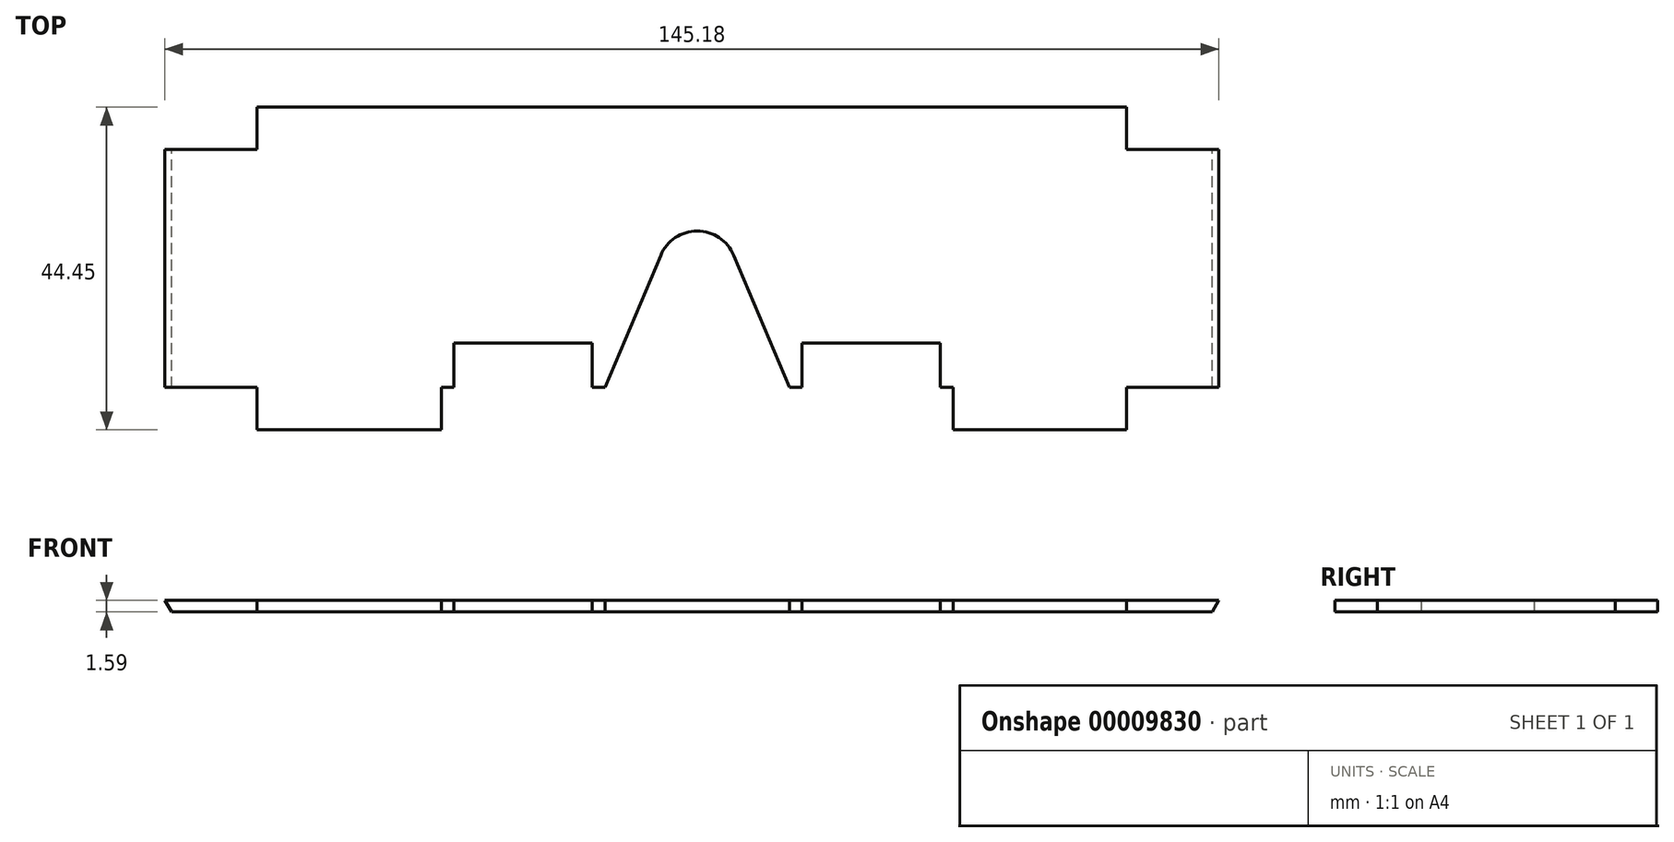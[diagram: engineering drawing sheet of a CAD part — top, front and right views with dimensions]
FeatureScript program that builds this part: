
annotation { "Feature Type Name" : "Feature", "Feature Type Description" : "" }
export const myFeature = defineFeature(function(context is Context, id is Id, definition is map)
    precondition{}
    {
        {
            var Q0;
            Q0=qCreatedBy(makeId("Top.planeOp"),FACE);
            var sketch = newSketch(context, id + "F0", { "sketchPlane" : qUnion([Q0])});
            skLineSegment(sketch, "E0.bottom", {"start": v(-125.55, -13.09) * mm, "end": v(19.63, -13.09) * mm});
            skLineSegment(sketch, "E0.top", {"start": v(-125.55, -57.54) * mm, "end": v(19.63, -57.54) * mm});
            skLineSegment(sketch, "E0.left", {"start": v(-125.55, -13.09) * mm, "end": v(-125.55, -57.54) * mm});
            skLineSegment(sketch, "E0.right", {"start": v(19.63, -13.09) * mm, "end": v(19.63, -57.54) * mm});
            skSolve(sketch);
        }
        {
            var Q0;
            Q0=qSketchRegion(id+"F0",true);
            extrude(context, id + "F1", {"entities" : qUnion([Q0]), "depth" : 1.59 * mm});
        }
        {
            var Q0;
            Q0=makeQuery(id+"F1.opExtrude","CAP_FACE",FACE,{"disambiguationData":[OSD([sQuery(id+"F0.wireOp",EDGE,"E0.bottom"),sQuery(id+"F0.wireOp",EDGE,"E0.top"),sQuery(id+"F0.wireOp",EDGE,"E0.left"),sQuery(id+"F0.wireOp",EDGE,"E0.right")])],"isStart":false});
            var sketch = newSketch(context, id + "F2", { "sketchPlane" : qUnion([Q0])});
            skLineSegment(sketch, "E1.bottom", {"start": v(-112.85, -13.09) * mm, "end": v(-87.45, -13.09) * mm});
            skLineSegment(sketch, "E1.left", {"start": v(-112.85, -13.09) * mm, "end": v(-112.85, -18.93) * mm});
            skLineSegment(sketch, "E2.bottom", {"start": v(-87.45, -13.09) * mm, "end": v(-87.45, -13.09) * mm});
            skLineSegment(sketch, "E3.bottom", {"start": v(-87.45, -13.09) * mm, "end": v(6.93, -13.09) * mm});
            skLineSegment(sketch, "E3.right", {"start": v(6.93, -13.09) * mm, "end": v(6.93, -18.93) * mm});
            skLineSegment(sketch, "E4.bottom", {"start": v(-112.85, -57.54) * mm, "end": v(-87.45, -57.54) * mm});
            skLineSegment(sketch, "E4.left", {"start": v(-112.85, -57.54) * mm, "end": v(-112.85, -51.7) * mm});
            skLineSegment(sketch, "E4.right", {"start": v(-87.45, -57.54) * mm, "end": v(-87.45, -51.7) * mm});
            skLineSegment(sketch, "E5.bottom", {"start": v(-64.92, -57.54) * mm, "end": v(-39.52, -57.54) * mm});
            skLineSegment(sketch, "E5.left", {"start": v(-64.92, -57.54) * mm, "end": v(-64.92, -51.7) * mm});
            skLineSegment(sketch, "E5.right", {"start": v(-39.52, -57.54) * mm, "end": v(-39.52, -51.7) * mm});
            skLineSegment(sketch, "E6.bottom", {"start": v(-17, -57.54) * mm, "end": v(6.93, -57.54) * mm});
            skLineSegment(sketch, "E6.left", {"start": v(-17, -57.54) * mm, "end": v(-17, -51.7) * mm});
            skLineSegment(sketch, "E6.right", {"start": v(6.93, -57.54) * mm, "end": v(6.93, -51.7) * mm});
            skPoint(sketch, "E7", {"position": v(-52.22, -18.93) * mm});
            skPoint(sketch, "E8", {"position": v(-52.22, -51.7) * mm});
            skLineSegment(sketch, "E9", {"start": v(-112.85, -18.93) * mm, "end": v(-125.55, -18.93) * mm});
            skLineSegment(sketch, "E10", {"start": v(-112.85, -51.7) * mm, "end": v(-125.55, -51.7) * mm});
            skLineSegment(sketch, "E11", {"start": v(-125.55, -51.7) * mm, "end": v(-125.55, -18.93) * mm});
            skLineSegment(sketch, "E12", {"start": v(6.93, -18.93) * mm, "end": v(19.63, -18.93) * mm});
            skLineSegment(sketch, "E13", {"start": v(6.93, -51.7) * mm, "end": v(19.63, -51.7) * mm});
            skLineSegment(sketch, "E14", {"start": v(19.63, -51.7) * mm, "end": v(19.63, -18.93) * mm});
            skLineSegment(sketch, "E15", {"start": v(-17, -51.7) * mm, "end": v(-39.52, -51.7) * mm});
            skLineSegment(sketch, "E16", {"start": v(-64.92, -51.7) * mm, "end": v(-87.45, -51.7) * mm});
            skSolve(sketch);
        }
        {
            var Q0;
            {var subQ4=sQuery(id+"F2.wireOp",EDGE,"E1.left");Q0=makeQuery(id+"F2.imprint","IMPRINT",FACE,{"disambiguationData":[TD([[makeQuery(id+"F2.imprint","IMPRINT",EDGE,{"derivedFrom":subQ4}),-1.0]])]});}
            var Q1;
            {var subQ2=sQuery(id+"F2.wireOp",EDGE,"E1.right");Q1=makeQuery(id+"F2.imprint","IMPRINT",FACE,{"disambiguationData":[TD([[makeQuery(id+"F2.imprint","IMPRINT",EDGE,{"derivedFrom":subQ2}),1.0]])]});}
            var Q2;
            {var subQ2=sQuery(id+"F2.wireOp",EDGE,"E2.right");Q2=makeQuery(id+"F2.imprint","IMPRINT",FACE,{"disambiguationData":[TD([[makeQuery(id+"F2.imprint","IMPRINT",EDGE,{"derivedFrom":subQ2}),1.0]])]});}
            var Q3;
            {var subQ4=sQuery(id+"F2.wireOp",EDGE,"E3.right");Q3=makeQuery(id+"F2.imprint","IMPRINT",FACE,{"disambiguationData":[TD([[makeQuery(id+"F2.imprint","IMPRINT",EDGE,{"derivedFrom":subQ4}),1.0]])]});}
            var Q4;
            {var subQ4=sQuery(id+"F2.wireOp",EDGE,"E6.right");Q4=makeQuery(id+"F2.imprint","IMPRINT",FACE,{"disambiguationData":[TD([[makeQuery(id+"F2.imprint","IMPRINT",EDGE,{"derivedFrom":subQ4}),-1.0]])]});}
            var Q5;
            {var subQ2=sQuery(id+"F2.wireOp",EDGE,"E5.right");Q5=makeQuery(id+"F2.imprint","IMPRINT",FACE,{"disambiguationData":[TD([[makeQuery(id+"F2.imprint","IMPRINT",EDGE,{"derivedFrom":subQ2}),-1.0]])]});}
            var Q6;
            {var subQ2=sQuery(id+"F2.wireOp",EDGE,"E4.right");Q6=makeQuery(id+"F2.imprint","IMPRINT",FACE,{"disambiguationData":[TD([[makeQuery(id+"F2.imprint","IMPRINT",EDGE,{"derivedFrom":subQ2}),-1.0]])]});}
            var Q7;
            {var subQ4=sQuery(id+"F2.wireOp",EDGE,"E4.left");Q7=makeQuery(id+"F2.imprint","IMPRINT",FACE,{"disambiguationData":[TD([[makeQuery(id+"F2.imprint","IMPRINT",EDGE,{"derivedFrom":subQ4}),1.0]])]});}
            var Q8;
            Q8=makeQuery(id+"F1.opExtrude","CAP_FACE",FACE,{"disambiguationData":[OSD([sQuery(id+"F0.wireOp",EDGE,"E0.bottom"),sQuery(id+"F0.wireOp",EDGE,"E0.top"),sQuery(id+"F0.wireOp",EDGE,"E0.left"),sQuery(id+"F0.wireOp",EDGE,"E0.right")])],"isStart":false});
            extrude(context, id + "F3", {"entities" : qUnion([Q0, Q1, Q2, Q3, Q4, Q5, Q6, Q7]), "operationType" : NewBodyOperationType.REMOVE, "endBound" : BoundingType.THROUGH_ALL, "oppositeDirection" : true, "endBoundEntityFace" : qUnion([Q8]), "depth" : 25.4 * mm});
        }
        {
            var Q0;
            Q0=makeQuery(id+"F1.opExtrude","CAP_FACE",FACE,{"disambiguationData":[OSD([sQuery(id+"F0.wireOp",EDGE,"E0.bottom"),sQuery(id+"F0.wireOp",EDGE,"E0.top"),sQuery(id+"F0.wireOp",EDGE,"E0.left"),sQuery(id+"F0.wireOp",EDGE,"E0.right")])],"isStart":true});
            var sketch = newSketch(context, id + "F4", { "sketchPlane" : qUnion([Q0])});
            skCircle(sketch, "E17", {"center": v(-52.22, 35.62) * mm, "radius": 5.46 * mm});
            skLineSegment(sketch, "E18", {"start": v(-57.26, 33.5) * mm, "end": v(-64.92, 51.7) * mm});
            skLineSegment(sketch, "E19", {"start": v(-47.19, 33.5) * mm, "end": v(-39.52, 51.7) * mm});
            skSolve(sketch);
        }
        {
            var Q0;
            Q0=makeQuery(id+"F4.imprint","IMPRINT",FACE,{"disambiguationData":[TD([[makeQuery(id+"F4.imprint","IMPRINT",EDGE,{"derivedFrom":sQuery(id+"F4.wireOp",EDGE,"E17")}),1.0]])]});
            var Q1;
            {var subQ0=sQuery(id+"F4.wireOp",EDGE,"E18");Q1=makeQuery(id+"F4.imprint","IMPRINT",FACE,{"disambiguationData":[TD([[makeQuery(id+"F4.imprint","IMPRINT",EDGE,{"derivedFrom":subQ0}),-1.0]])]});}
            extrude(context, id + "F5", {"entities" : qUnion([Q0, Q1]), "operationType" : NewBodyOperationType.REMOVE, "endBound" : BoundingType.THROUGH_ALL, "oppositeDirection" : true, "depth" : 25.4 * mm});
        }
        {
            var Q0;
            Q0=makeQuery(id+"F1.opExtrude","CAP_FACE",FACE,{"disambiguationData":[OSD([sQuery(id+"F0.wireOp",EDGE,"E0.bottom"),sQuery(id+"F0.wireOp",EDGE,"E0.top"),sQuery(id+"F0.wireOp",EDGE,"E0.left"),sQuery(id+"F0.wireOp",EDGE,"E0.right")])],"isStart":false});
            var sketch = newSketch(context, id + "F6", { "sketchPlane" : qUnion([Q0])});
            skLineSegment(sketch, "E20.bottom", {"start": v(-85.71, -45.6) * mm, "end": v(-66.66, -45.6) * mm});
            skLineSegment(sketch, "E20.top", {"start": v(-85.71, -51.7) * mm, "end": v(-66.66, -51.7) * mm});
            skLineSegment(sketch, "E20.left", {"start": v(-85.71, -45.6) * mm, "end": v(-85.71, -51.7) * mm});
            skLineSegment(sketch, "E20.right", {"start": v(-66.66, -45.6) * mm, "end": v(-66.66, -51.7) * mm});
            skPoint(sketch, "E21", {"position": v(-76.19, -45.6) * mm});
            skLineSegment(sketch, "E22.bottom", {"start": v(-37.78, -45.6) * mm, "end": v(-18.73, -45.6) * mm});
            skLineSegment(sketch, "E22.top", {"start": v(-37.78, -51.7) * mm, "end": v(-18.73, -51.7) * mm});
            skLineSegment(sketch, "E22.left", {"start": v(-37.78, -45.6) * mm, "end": v(-37.78, -51.7) * mm});
            skLineSegment(sketch, "E22.right", {"start": v(-18.73, -45.6) * mm, "end": v(-18.73, -51.7) * mm});
            skPoint(sketch, "E23", {"position": v(-28.26, -51.7) * mm});
            skPoint(sketch, "E24", {"position": v(-76.19, -51.7) * mm});
            skSolve(sketch);
        }
        {
            var Q0;
            Q0=makeQuery(id+"F6.imprint","IMPRINT",FACE,{"disambiguationData":[TD([[makeQuery(id+"F6.imprint","IMPRINT",EDGE,{"derivedFrom":sQuery(id+"F6.wireOp",EDGE,"E20.bottom")}),-1.0]])]});
            var Q1;
            Q1=makeQuery(id+"F6.imprint","IMPRINT",FACE,{"disambiguationData":[TD([[makeQuery(id+"F6.imprint","IMPRINT",EDGE,{"derivedFrom":sQuery(id+"F6.wireOp",EDGE,"E22.bottom")}),-1.0]])]});
            extrude(context, id + "F7", {"entities" : qUnion([Q0, Q1]), "operationType" : NewBodyOperationType.REMOVE, "endBound" : BoundingType.THROUGH_ALL, "oppositeDirection" : true, "depth" : 25.4 * mm});
        }
        {
            var Q0;
            Q0=makeQuery(id+"F3.boolean.opBoolean","COPY",FACE,{"derivedFrom":makeQuery(id+"F3.opExtrude","SWEPT_FACE",FACE,{"disambiguationData":[OSD([sQuery(id+"F2.wireOp",EDGE,"E12")])]})});
            var sketch = newSketch(context, id + "F8", { "sketchPlane" : qUnion([Q0])});
            skLineSegment(sketch, "E25", {"start": v(-19.63, 1.59) * mm, "end": v(-18.72, 0) * mm});
            skLineSegment(sketch, "E26", {"start": v(-18.72, 0) * mm, "end": v(-18.72, 1.59) * mm});
            skLineSegment(sketch, "E27", {"start": v(-18.72, 1.59) * mm, "end": v(-19.63, 1.59) * mm});
            skSolve(sketch);
        }
        {
            var Q0;
            Q0=makeQuery(id+"F3.boolean.opBoolean","COPY",FACE,{"derivedFrom":makeQuery(id+"F3.opExtrude","SWEPT_FACE",FACE,{"disambiguationData":[OSD([sQuery(id+"F2.wireOp",EDGE,"E9")])]})});
            var sketch = newSketch(context, id + "F9", { "sketchPlane" : qUnion([Q0])});
            skLineSegment(sketch, "E28", {"start": v(125.55, 1.59) * mm, "end": v(124.64, 0) * mm});
            skLineSegment(sketch, "E29", {"start": v(124.64, 0) * mm, "end": v(124.64, 1.59) * mm});
            skLineSegment(sketch, "E30", {"start": v(124.64, 1.59) * mm, "end": v(125.55, 1.59) * mm});
            skSolve(sketch);
        }
        {
            var Q0;
            {var subQ3=sQuery(id+"F9.wireOp",EDGE,"E28");Q0=makeQuery(id+"F9.imprint","IMPRINT",FACE,{"disambiguationData":[TD([[makeQuery(id+"F9.imprint","IMPRINT",EDGE,{"derivedFrom":subQ3}),1.0]])]});}
            var Q1;
            {var subQ3=sQuery(id+"F8.wireOp",EDGE,"E25");Q1=makeQuery(id+"F8.imprint","IMPRINT",FACE,{"disambiguationData":[TD([[makeQuery(id+"F8.imprint","IMPRINT",EDGE,{"derivedFrom":subQ3}),-1.0]])]});}
            extrude(context, id + "F10", {"entities" : qUnion([Q0, Q1]), "operationType" : NewBodyOperationType.REMOVE, "endBound" : BoundingType.THROUGH_ALL, "oppositeDirection" : true, "depth" : 25.4 * mm});
        }
    });
